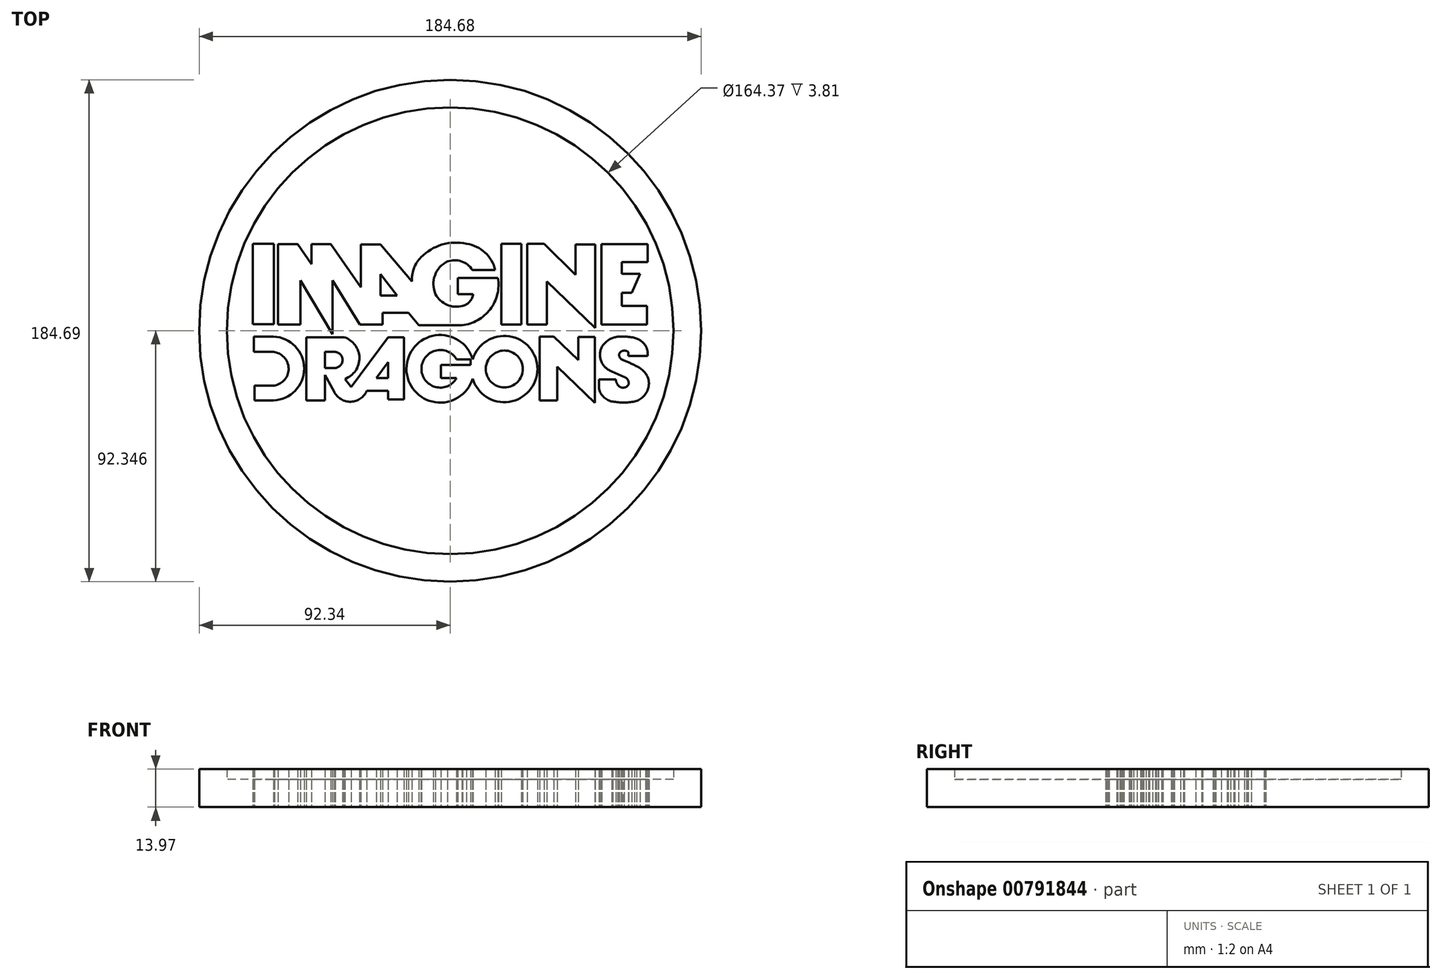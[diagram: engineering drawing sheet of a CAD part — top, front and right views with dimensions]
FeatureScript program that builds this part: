
annotation { "Feature Type Name" : "Feature", "Feature Type Description" : "" }
export const myFeature = defineFeature(function(context is Context, id is Id, definition is map)
    precondition{}
    {
        {
            var Q0;
            Q0=qCreatedBy(makeId("Top.planeOp"),FACE);
            var sketch = newSketch(context, id + "F0", { "sketchPlane" : qUnion([Q0])});
            skLineSegment(sketch, "E0.bottom", {"start": v(-72.66, 28.51) * mm, "end": v(-64.9, 28.51) * mm});
            skLineSegment(sketch, "E0.top", {"start": v(-72.66, -1.04) * mm, "end": v(-64.9, -1.04) * mm});
            skLineSegment(sketch, "E0.left", {"start": v(-72.66, 28.51) * mm, "end": v(-72.66, -1.04) * mm});
            skLineSegment(sketch, "E0.right", {"start": v(-64.9, 28.51) * mm, "end": v(-64.9, -1.04) * mm});
            skLineSegment(sketch, "E1.bottom", {"start": v(-63.32, 28.36) * mm, "end": v(-56.14, 28.36) * mm});
            skLineSegment(sketch, "E1.top", {"start": v(-63.32, -1.18) * mm, "end": v(-55.1, -1.18) * mm});
            skLineSegment(sketch, "E1.left", {"start": v(-63.32, 28.36) * mm, "end": v(-63.32, -1.18) * mm});
            skLineSegment(sketch, "E1.right", {"start": v(-55.1, 15.1) * mm, "end": v(-55.1, -1.18) * mm});
            skLineSegment(sketch, "E2.bottom", {"start": v(-32.81, 28.22) * mm, "end": v(-25.57, 28.22) * mm});
            skLineSegment(sketch, "E2.top", {"start": v(-32.81, -1.18) * mm, "end": v(-25.57, -1.18) * mm});
            skLineSegment(sketch, "E2.left", {"start": v(-32.81, 28.22) * mm, "end": v(-32.81, 12.5) * mm});
            skLineSegment(sketch, "E2.right", {"start": v(-25.57, 17.37) * mm, "end": v(-25.57, 9.44) * mm});
            skLineSegment(sketch, "E3.bottom", {"start": v(18.88, 28.5) * mm, "end": v(26.26, 28.5) * mm});
            skLineSegment(sketch, "E3.top", {"start": v(18.88, -1.18) * mm, "end": v(26.26, -1.18) * mm});
            skLineSegment(sketch, "E3.left", {"start": v(18.88, 28.5) * mm, "end": v(18.88, -1.18) * mm});
            skLineSegment(sketch, "E3.right", {"start": v(26.26, 28.5) * mm, "end": v(26.26, -1.18) * mm});
            skLineSegment(sketch, "E4.top", {"start": v(28.35, -1.18) * mm, "end": v(35.6, -1.18) * mm});
            skLineSegment(sketch, "E4.left", {"start": v(28.35, 28.5) * mm, "end": v(28.35, -1.18) * mm});
            skLineSegment(sketch, "E5.bottom", {"start": v(55.66, 28.36) * mm, "end": v(63.18, 28.36) * mm});
            skLineSegment(sketch, "E5.top", {"start": v(55.66, -1.18) * mm, "end": v(63.18, -1.18) * mm});
            skLineSegment(sketch, "E5.left", {"start": v(55.66, 28.36) * mm, "end": v(55.66, -1.18) * mm});
            skLineSegment(sketch, "E5.right", {"start": v(63.18, 21.8) * mm, "end": v(63.18, 17.49) * mm});
            skLineSegment(sketch, "E6.bottom", {"start": v(72.66, 21.8) * mm, "end": v(63.18, 21.8) * mm});
            skLineSegment(sketch, "E6.top", {"start": v(72.66, 28.36) * mm, "end": v(55.66, 28.36) * mm});
            skLineSegment(sketch, "E6.left", {"start": v(72.66, 21.8) * mm, "end": v(72.66, 28.36) * mm});
            skLineSegment(sketch, "E6.right", {"start": v(55.66, 21.8) * mm, "end": v(55.66, 28.36) * mm});
            skLineSegment(sketch, "E7.bottom", {"start": v(72.38, 5.65) * mm, "end": v(63.18, 5.65) * mm});
            skLineSegment(sketch, "E7.top", {"start": v(72.38, -1.18) * mm, "end": v(55.66, -1.18) * mm});
            skLineSegment(sketch, "E7.left", {"start": v(72.38, 5.65) * mm, "end": v(72.38, -1.18) * mm});
            skLineSegment(sketch, "E7.right", {"start": v(55.66, 5.65) * mm, "end": v(55.66, -1.18) * mm});
            skLineSegment(sketch, "E8.bottom", {"start": v(69.87, 17.49) * mm, "end": v(63.18, 17.49) * mm});
            skLineSegment(sketch, "E8.top", {"start": v(66.8, 10.52) * mm, "end": v(63.18, 10.52) * mm});
            skLineSegment(sketch, "E8.right", {"start": v(55.66, 17.49) * mm, "end": v(55.66, 10.52) * mm});
            skLineSegment(sketch, "E9", {"start": v(69.87, 17.49) * mm, "end": v(66.8, 10.52) * mm});
            skLineSegment(sketch, "E10.trimOffspring", {"start": v(63.18, 10.52) * mm, "end": v(63.18, 5.65) * mm});
            skLineSegment(sketch, "E11.bottom", {"start": v(2.86, 15.96) * mm, "end": v(17.62, 15.96) * mm});
            skLineSegment(sketch, "E11.top", {"start": v(2.86, 9.96) * mm, "end": v(8.49, 9.96) * mm});
            skLineSegment(sketch, "E11.left", {"start": v(2.86, 15.96) * mm, "end": v(2.86, 9.96) * mm});
            skArc(sketch, "E12", {"start": v(4.39, -1.46) * mm, "mid": v(14.74, 4.4) * mm, "end": v(17.62, 15.96) * mm});
            skArc(sketch, "E13", {"start": v(4.64, 5.64) * mm, "mid": v(7.22, 7.21) * mm, "end": v(8.49, 9.96) * mm});
            skArc(sketch, "E14", {"start": v(-5.39, 10) * mm, "mid": v(-1.14, 6.04) * mm, "end": v(4.64, 5.64) * mm});
            skArc(sketch, "E15", {"start": v(-1, 21.96) * mm, "mid": v(-5.6, 16.86) * mm, "end": v(-5.39, 10) * mm});
            skArc(sketch, "E16", {"start": v(8.2, 18.86) * mm, "mid": v(4.15, 22.05) * mm, "end": v(-1, 21.96) * mm});
            skLineSegment(sketch, "E17", {"start": v(8.2, 18.86) * mm, "end": v(16.6, 18.86) * mm});
            skArc(sketch, "E18", {"start": v(16.6, 18.86) * mm, "mid": v(12.8, 25.29) * mm, "end": v(6.05, 28.5) * mm});
            skArc(sketch, "E19", {"start": v(6.05, 28.5) * mm, "mid": v(-2.97, 28.2) * mm, "end": v(-10.7, 23.53) * mm});
            skArc(sketch, "E20", {"start": v(-10.7, 23.53) * mm, "mid": v(-13.34, 19.43) * mm, "end": v(-14.05, 14.61) * mm});
            skLineSegment(sketch, "E21", {"start": v(-25.57, 28.22) * mm, "end": v(-14.05, 14.61) * mm});
            skLineSegment(sketch, "E22", {"start": v(-25.57, 17.37) * mm, "end": v(-19.56, 9.44) * mm});
            skLineSegment(sketch, "E23", {"start": v(-19.56, 9.44) * mm, "end": v(-25.57, 9.44) * mm});
            skLineSegment(sketch, "E24", {"start": v(-25.57, -1.18) * mm, "end": v(-24.78, -1.18) * mm});
            skLineSegment(sketch, "E25", {"start": v(-24.78, -1.18) * mm, "end": v(-24.78, 3.13) * mm});
            skLineSegment(sketch, "E26", {"start": v(-24.78, 3.13) * mm, "end": v(-15.32, 3.13) * mm});
            skLineSegment(sketch, "E27", {"start": v(4.39, -1.46) * mm, "end": v(-11.51, -1.46) * mm});
            skLineSegment(sketch, "E28", {"start": v(-11.51, -1.46) * mm, "end": v(-15.32, 3.13) * mm});
            skLineSegment(sketch, "E29", {"start": v(53.35, -2.52) * mm, "end": v(35.6, 14.71) * mm});
            skLineSegment(sketch, "E30", {"start": v(35.6, 14.71) * mm, "end": v(53.35, -2.52) * mm});
            skLineSegment(sketch, "E31", {"start": v(53.35, -2.52) * mm, "end": v(53.35, 28.22) * mm});
            skLineSegment(sketch, "E32", {"start": v(53.35, 28.22) * mm, "end": v(46.14, 28.22) * mm});
            skLineSegment(sketch, "E33", {"start": v(46.14, 28.22) * mm, "end": v(46.14, 17.03) * mm});
            skLineSegment(sketch, "E34", {"start": v(46.14, 17.03) * mm, "end": v(34.55, 28.5) * mm});
            skLineSegment(sketch, "E35.trimOffspring", {"start": v(35.6, 14.71) * mm, "end": v(35.6, -1.18) * mm});
            skLineSegment(sketch, "E36", {"start": v(34.55, 28.5) * mm, "end": v(28.35, 28.5) * mm});
            skLineSegment(sketch, "E37", {"start": v(-43.95, 28.4) * mm, "end": v(-51.06, 28.4) * mm});
            skLineSegment(sketch, "E38", {"start": v(-51.06, 28.4) * mm, "end": v(-51.06, 20.95) * mm});
            skLineSegment(sketch, "E39", {"start": v(-51.06, 20.95) * mm, "end": v(-56.14, 28.36) * mm});
            skLineSegment(sketch, "E40", {"start": v(-43.95, 28.4) * mm, "end": v(-32.81, 12.5) * mm});
            skLineSegment(sketch, "E41", {"start": v(-32.81, -1.18) * mm, "end": v(-33.26, -1.18) * mm});
            skLineSegment(sketch, "E42", {"start": v(-33.26, -1.18) * mm, "end": v(-43.22, 15.1) * mm});
            skLineSegment(sketch, "E43", {"start": v(-55.1, 15.1) * mm, "end": v(-43.22, -4.8) * mm});
            skLineSegment(sketch, "E44", {"start": v(-43.22, -4.8) * mm, "end": v(-43.22, 15.1) * mm});
            skCircle(sketch, "E45", {"center": v(19.96, -17.6) * mm, "radius": 6.8 * mm});
            skArc(sketch, "E46", {"start": v(2.34, -14.03) * mm, "mid": v(-10.54, -17.53) * mm, "end": v(2.36, -20.96) * mm});
            skArc(sketch, "E47", {"start": v(8.28, -21.11) * mm, "mid": v(32.15, -17.63) * mm, "end": v(8.3, -14) * mm});
            skArc(sketch, "E48", {"start": v(8.3, -14) * mm, "mid": v(-16.07, -17.47) * mm, "end": v(8.28, -21.11) * mm});
            skLineSegment(sketch, "E49", {"start": v(-3.35, -20.96) * mm, "end": v(2.36, -20.96) * mm});
            skLineSegment(sketch, "E50", {"start": v(-3.35, -20.96) * mm, "end": v(-3.35, -16.05) * mm});
            skLineSegment(sketch, "E51", {"start": v(-3.35, -16.05) * mm, "end": v(7.55, -16.05) * mm});
            skLineSegment(sketch, "E52", {"start": v(7.55, -16.05) * mm, "end": v(7.55, -14.03) * mm});
            skLineSegment(sketch, "E53", {"start": v(7.55, -14.03) * mm, "end": v(2.34, -14.03) * mm});
            skLineSegment(sketch, "E54.bottom", {"start": v(-16.92, -5.9) * mm, "end": v(-22.82, -5.9) * mm});
            skLineSegment(sketch, "E54.top", {"start": v(-16.92, -28.72) * mm, "end": v(-22.82, -28.72) * mm});
            skLineSegment(sketch, "E54.left", {"start": v(-16.92, -5.9) * mm, "end": v(-16.92, -28.72) * mm});
            skLineSegment(sketch, "E54.right", {"start": v(-22.82, -15.12) * mm, "end": v(-22.82, -20.85) * mm});
            skLineSegment(sketch, "E55", {"start": v(-22.82, -5.9) * mm, "end": v(-36.42, -24.19) * mm});
            skLineSegment(sketch, "E56", {"start": v(-22.82, -15.12) * mm, "end": v(-27.08, -20.85) * mm});
            skLineSegment(sketch, "E57", {"start": v(-27.08, -20.85) * mm, "end": v(-22.82, -20.85) * mm});
            skLineSegment(sketch, "E58", {"start": v(-30.64, -25.55) * mm, "end": v(-22.82, -25.55) * mm});
            skArc(sketch, "E59", {"start": v(-42.66, -25.93) * mm, "mid": v(-36.53, -29.63) * mm, "end": v(-30.64, -25.55) * mm});
            skLineSegment(sketch, "E60", {"start": v(-42.66, -25.93) * mm, "end": v(-46, -19.8) * mm});
            skLineSegment(sketch, "E61", {"start": v(-46, -19.8) * mm, "end": v(-46, -29.12) * mm});
            skLineSegment(sketch, "E62", {"start": v(-46, -29.12) * mm, "end": v(-52.9, -29.12) * mm});
            skLineSegment(sketch, "E63", {"start": v(-52.9, -29.12) * mm, "end": v(-52.9, -5.87) * mm});
            skLineSegment(sketch, "E64", {"start": v(-52.9, -5.87) * mm, "end": v(-39, -5.87) * mm});
            skArc(sketch, "E65", {"start": v(-38.71, -21.24) * mm, "mid": v(-33.37, -13.45) * mm, "end": v(-39, -5.87) * mm});
            skLineSegment(sketch, "E66", {"start": v(-36.42, -24.19) * mm, "end": v(-38.71, -21.24) * mm});
            skLineSegment(sketch, "E67", {"start": v(-46.07, -11.3) * mm, "end": v(-46.07, -17.23) * mm});
            skLineSegment(sketch, "E68", {"start": v(-46.07, -17.23) * mm, "end": v(-42.55, -17.23) * mm});
            skLineSegment(sketch, "E69", {"start": v(-46.07, -11.3) * mm, "end": v(-42.28, -11.3) * mm});
            skArc(sketch, "E70", {"start": v(-42.55, -17.23) * mm, "mid": v(-39.59, -14.4) * mm, "end": v(-42.28, -11.3) * mm});
            skArc(sketch, "E71", {"start": v(-64.61, -23.63) * mm, "mid": v(-59.42, -17.29) * mm, "end": v(-65.03, -11.3) * mm});
            skArc(sketch, "E72", {"start": v(-65.03, -29.14) * mm, "mid": v(-53.72, -17.4) * mm, "end": v(-65.03, -5.66) * mm});
            skLineSegment(sketch, "E73", {"start": v(-65.03, -5.66) * mm, "end": v(-72.2, -5.66) * mm});
            skLineSegment(sketch, "E74", {"start": v(-72.2, -5.66) * mm, "end": v(-72.2, -11.3) * mm});
            skLineSegment(sketch, "E75", {"start": v(-72.2, -11.3) * mm, "end": v(-65.03, -11.3) * mm});
            skLineSegment(sketch, "E76", {"start": v(-64.61, -23.63) * mm, "end": v(-72, -23.63) * mm});
            skLineSegment(sketch, "E77", {"start": v(-65.03, -29.14) * mm, "end": v(-71.93, -29.14) * mm});
            skLineSegment(sketch, "E78", {"start": v(-71.93, -29.14) * mm, "end": v(-72, -23.63) * mm});
            skLineSegment(sketch, "E79.trimOffspring", {"start": v(-22.82, -25.55) * mm, "end": v(-22.82, -28.72) * mm});
            skLineSegment(sketch, "E80.bottom", {"start": v(32.9, -5.66) * mm, "end": v(38.11, -5.66) * mm});
            skLineSegment(sketch, "E80.top", {"start": v(32.9, -29.19) * mm, "end": v(39.35, -29.19) * mm});
            skLineSegment(sketch, "E80.left", {"start": v(32.9, -5.66) * mm, "end": v(32.9, -29.19) * mm});
            skLineSegment(sketch, "E81", {"start": v(38.11, -5.66) * mm, "end": v(47.22, -14.27) * mm});
            skLineSegment(sketch, "E82", {"start": v(47.22, -14.27) * mm, "end": v(47.22, -5.82) * mm});
            skLineSegment(sketch, "E83", {"start": v(47.22, -5.82) * mm, "end": v(53.27, -5.82) * mm});
            skLineSegment(sketch, "E84", {"start": v(53.27, -5.82) * mm, "end": v(53.27, -30.01) * mm});
            skLineSegment(sketch, "E85", {"start": v(53.27, -30.01) * mm, "end": v(39.35, -16.68) * mm});
            skLineSegment(sketch, "E86.trimOffspring", {"start": v(39.35, -16.68) * mm, "end": v(39.35, -29.19) * mm});
            skArc(sketch, "E87", {"start": v(62.9, -13.95) * mm, "mid": v(63.25, -14.14) * mm, "end": v(63.65, -14.26) * mm});
            skArc(sketch, "E88", {"start": v(61.7, -23.4) * mm, "mid": v(63.66, -24.46) * mm, "end": v(65.6, -23.37) * mm});
            skLineSegment(sketch, "E89", {"start": v(60.95, -21.36) * mm, "end": v(54.78, -21.36) * mm});
            skLineSegment(sketch, "E90", {"start": v(54.78, -21.36) * mm, "end": v(54.78, -24.8) * mm});
            skArc(sketch, "E91", {"start": v(54.78, -24.8) * mm, "mid": v(56.58, -27.99) * mm, "end": v(59.87, -29.58) * mm});
            skArc(sketch, "E92", {"start": v(59.87, -29.58) * mm, "mid": v(63.84, -29.92) * mm, "end": v(67.81, -29.58) * mm});
            skArc(sketch, "E93", {"start": v(67.81, -29.58) * mm, "mid": v(70.97, -27.88) * mm, "end": v(72.83, -24.8) * mm});
            skArc(sketch, "E94", {"start": v(72.83, -24.8) * mm, "mid": v(73.14, -22.87) * mm, "end": v(72.83, -20.94) * mm});
            skArc(sketch, "E95", {"start": v(72.83, -20.94) * mm, "mid": v(71.18, -18.35) * mm, "end": v(68.68, -16.59) * mm});
            skArc(sketch, "E96", {"start": v(68.68, -16.59) * mm, "mid": v(65.82, -15.2) * mm, "end": v(62.9, -13.95) * mm});
            skArc(sketch, "E97", {"start": v(60.95, -21.36) * mm, "mid": v(61.2, -22.43) * mm, "end": v(61.7, -23.4) * mm});
            skArc(sketch, "E98", {"start": v(65.6, -23.37) * mm, "mid": v(65.43, -21.63) * mm, "end": v(64.05, -20.56) * mm});
            skLineSegment(sketch, "E99", {"start": v(64.05, -20.56) * mm, "end": v(59.52, -18.43) * mm});
            skArc(sketch, "E100", {"start": v(55.83, -9.52) * mm, "mid": v(55.65, -14.82) * mm, "end": v(59.52, -18.43) * mm});
            skArc(sketch, "E101", {"start": v(61.61, -5.69) * mm, "mid": v(58.28, -6.94) * mm, "end": v(55.83, -9.52) * mm});
            skArc(sketch, "E102", {"start": v(71.88, -8.98) * mm, "mid": v(69.71, -6.9) * mm, "end": v(66.87, -5.93) * mm});
            skArc(sketch, "E103", {"start": v(66.87, -5.93) * mm, "mid": v(64.25, -5.63) * mm, "end": v(61.61, -5.69) * mm});
            skLineSegment(sketch, "E104", {"start": v(65.58, -11.35) * mm, "end": v(65.58, -12.8) * mm});
            skArc(sketch, "E105", {"start": v(65.58, -11.35) * mm, "mid": v(63.88, -10.81) * mm, "end": v(62.34, -11.71) * mm});
            skArc(sketch, "E106", {"start": v(62.34, -11.71) * mm, "mid": v(62.26, -12.92) * mm, "end": v(62.9, -13.95) * mm});
            skLineSegment(sketch, "E107", {"start": v(65.58, -12.8) * mm, "end": v(72.72, -12.8) * mm});
            skArc(sketch, "E108", {"start": v(72.72, -12.8) * mm, "mid": v(72.61, -10.82) * mm, "end": v(71.88, -8.98) * mm});
            skCircle(sketch, "E109", {"center": v(0, -3.5) * mm, "radius": 82.18 * mm});
            skCircle(sketch, "E110", {"center": v(0, -3.5) * mm, "radius": 92.34 * mm});
            skSolve(sketch);
        }
        {
            var Q0;
            Q0=makeQuery(id+"F0.imprint","IMPRINT",FACE,{"disambiguationData":[TD([[makeQuery(id+"F0.imprint","IMPRINT",EDGE,{"derivedFrom":sQuery(id+"F0.wireOp",EDGE,"E0.bottom")}),1.0]])]});
            var Q1;
            Q1=makeQuery(id+"F0.imprint","IMPRINT",FACE,{"disambiguationData":[TD([[makeQuery(id+"F0.imprint","IMPRINT",EDGE,{"derivedFrom":sQuery(id+"F0.wireOp",EDGE,"E2.right")}),1.0]])]});
            var Q2;
            Q2=makeQuery(id+"F0.imprint","IMPRINT",FACE,{"disambiguationData":[TD([[makeQuery(id+"F0.imprint","IMPRINT",EDGE,{"derivedFrom":sQuery(id+"F0.wireOp",EDGE,"E67")}),1.0]])]});
            var Q3;
            Q3=makeQuery(id+"F0.imprint","IMPRINT",FACE,{"disambiguationData":[TD([[makeQuery(id+"F0.imprint","IMPRINT",EDGE,{"derivedFrom":sQuery(id+"F0.wireOp",EDGE,"E54.right")}),-1.0]])]});
            var Q4;
            Q4=makeQuery(id+"F0.imprint","IMPRINT",FACE,{"disambiguationData":[TD([[makeQuery(id+"F0.imprint","IMPRINT",EDGE,{"derivedFrom":sQuery(id+"F0.wireOp",EDGE,"E46")}),1.0]])]});
            var Q5;
            Q5=makeQuery(id+"F0.imprint","IMPRINT",FACE,{"disambiguationData":[TD([[makeQuery(id+"F0.imprint","IMPRINT",EDGE,{"derivedFrom":sQuery(id+"F0.wireOp",EDGE,"E45")}),1.0]])]});
            extrude(context, id + "F1", {"entities" : qUnion([Q0, Q1, Q2, Q3, Q4, Q5]), "depth" : 10.16 * mm, "offsetDistance" : 25.4 * mm});
        }
        {
            var Q0;
            Q0=makeQuery(id+"F0.imprint","IMPRINT",FACE,{"disambiguationData":[TD([[makeQuery(id+"F0.imprint","IMPRINT",EDGE,{"derivedFrom":sQuery(id+"F0.wireOp",EDGE,"E1.bottom")}),-1.0]])]});
            var Q1;
            Q1=makeQuery(id+"F0.imprint","IMPRINT",FACE,{"disambiguationData":[TD([[makeQuery(id+"F0.imprint","IMPRINT",EDGE,{"derivedFrom":sQuery(id+"F0.wireOp",EDGE,"E0.bottom")}),-1.0]])]});
            var Q2;
            Q2=makeQuery(id+"F0.imprint","IMPRINT",FACE,{"disambiguationData":[TD([[makeQuery(id+"F0.imprint","IMPRINT",EDGE,{"derivedFrom":sQuery(id+"F0.wireOp",EDGE,"E71")}),-1.0]])]});
            var Q3;
            Q3=makeQuery(id+"F0.imprint","IMPRINT",FACE,{"disambiguationData":[TD([[makeQuery(id+"F0.imprint","IMPRINT",EDGE,{"derivedFrom":sQuery(id+"F0.wireOp",EDGE,"E54.bottom")}),1.0]])]});
            var Q4;
            Q4=makeQuery(id+"F0.imprint","IMPRINT",FACE,{"disambiguationData":[TD([[makeQuery(id+"F0.imprint","IMPRINT",EDGE,{"derivedFrom":sQuery(id+"F0.wireOp",EDGE,"E45")}),-1.0]])]});
            var Q5;
            Q5=makeQuery(id+"F0.imprint","IMPRINT",FACE,{"disambiguationData":[TD([[makeQuery(id+"F0.imprint","IMPRINT",EDGE,{"derivedFrom":sQuery(id+"F0.wireOp",EDGE,"E80.bottom")}),-1.0]])]});
            var Q6;
            {var subQ1=sQuery(id+"F0.wireOp",EDGE,"E87");Q6=makeQuery(id+"F0.imprint","IMPRINT",FACE,{"disambiguationData":[TD([[makeQuery(id+"F0.imprint","IMPRINT",EDGE,{"derivedFrom":subQ1}),-1.0]])]});}
            var Q7;
            Q7=makeQuery(id+"F0.imprint","IMPRINT",FACE,{"disambiguationData":[TD([[makeQuery(id+"F0.imprint","IMPRINT",EDGE,{"derivedFrom":sQuery(id+"F0.wireOp",EDGE,"E5.right")}),-1.0]])]});
            var Q8;
            Q8=makeQuery(id+"F0.imprint","IMPRINT",FACE,{"disambiguationData":[TD([[makeQuery(id+"F0.imprint","IMPRINT",EDGE,{"derivedFrom":sQuery(id+"F0.wireOp",EDGE,"E4.top")}),1.0]])]});
            var Q9;
            Q9=makeQuery(id+"F0.imprint","IMPRINT",FACE,{"disambiguationData":[TD([[makeQuery(id+"F0.imprint","IMPRINT",EDGE,{"derivedFrom":sQuery(id+"F0.wireOp",EDGE,"E3.bottom")}),-1.0]])]});
            extrude(context, id + "F2", {"entities" : qUnion([Q0, Q1, Q2, Q3, Q4, Q5, Q6, Q7, Q8, Q9]), "depth" : 13.97 * mm, "offsetDistance" : 25.4 * mm});
        }
        {
            var Q0;
            Q0=makeQuery(id+"F0.imprint","IMPRINT",FACE,{"disambiguationData":[TD([[makeQuery(id+"F0.imprint","IMPRINT",EDGE,{"derivedFrom":sQuery(id+"F0.wireOp",EDGE,"E109")}),-1.0]])]});
            extrude(context, id + "F3", {"entities" : qUnion([Q0]), "operationType" : NewBodyOperationType.ADD, "depth" : 13.97 * mm, "offsetDistance" : 25.4 * mm});
        }
    });
